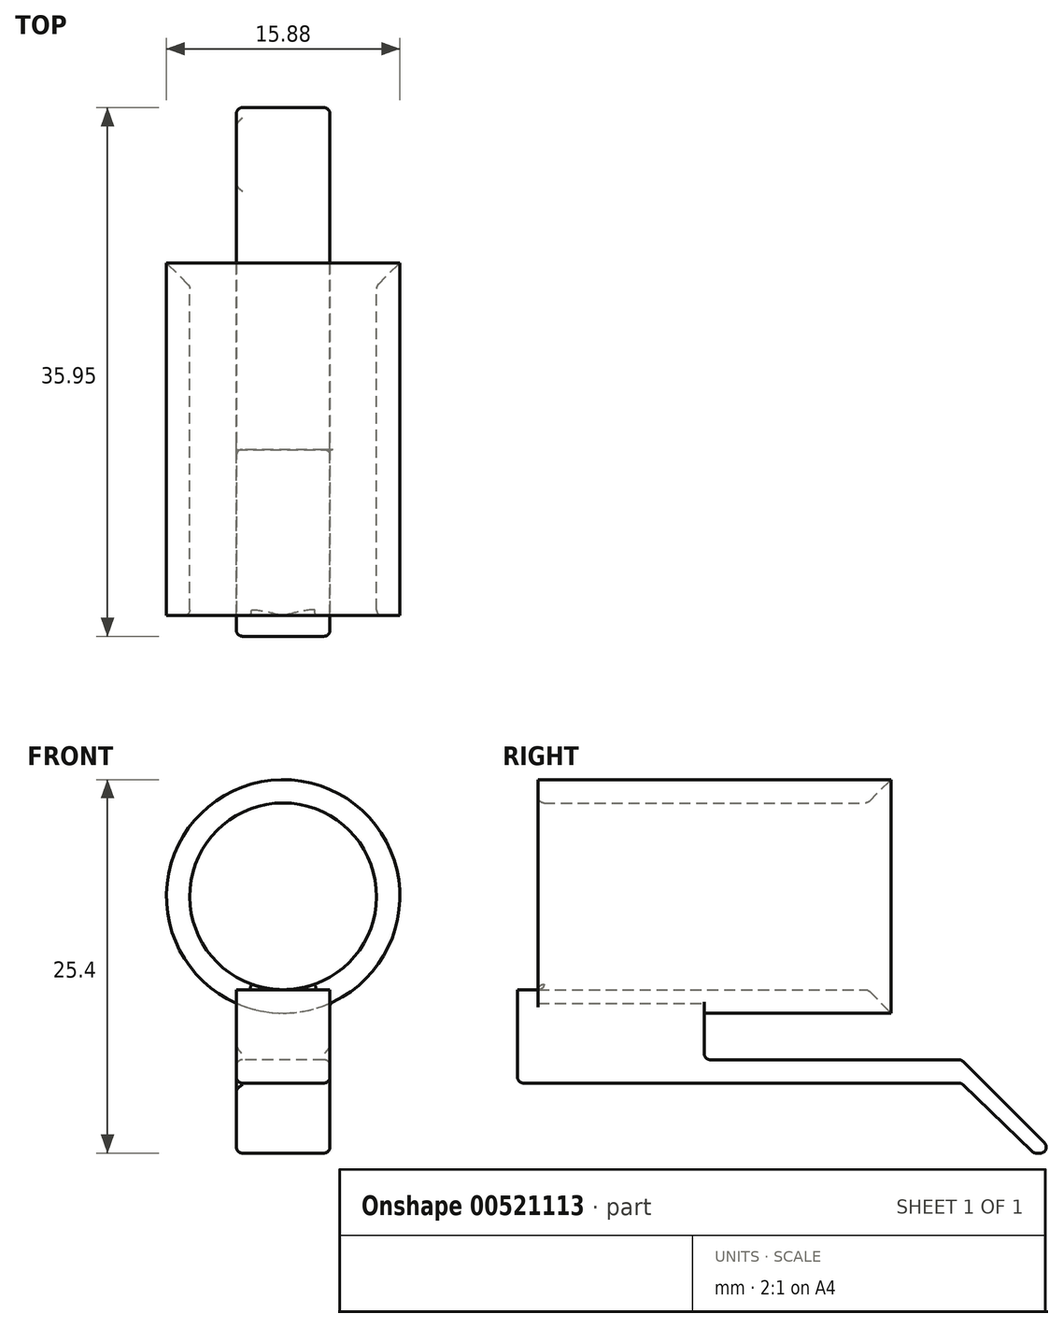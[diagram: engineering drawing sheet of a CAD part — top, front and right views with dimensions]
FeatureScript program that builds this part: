
annotation { "Feature Type Name" : "Feature", "Feature Type Description" : "" }
export const myFeature = defineFeature(function(context is Context, id is Id, definition is map)
    precondition{}
    {
        {
            var Q0;
            Q0=qCreatedBy(makeId("Front.planeOp"),FACE);
            var sketch = newSketch(context, id + "F0", { "sketchPlane" : qUnion([Q0])});
            skCircle(sketch, "E0", {"center": v(0, 0) * mm, "radius": 6.35 * mm});
            skCircle(sketch, "E1", {"center": v(0, 0) * mm, "radius": 7.94 * mm});
            skLineSegment(sketch, "E2", {"start": v(3.42, 5.35) * mm, "end": v(4.28, 6.69) * mm, "construction": true});
            skSolve(sketch);
        }
        {
            assignVariable(context, id + "F1", {"name" : "BarrelLenght", "anyValue" : 24});
        }
        {
            var Q0;
            Q0 = qSketchRegion(id + "F0", true);
            extrude(context, id + "F2", {"entities" : qUnion([Q0]), "depth" : (getVariable(context, 'BarrelLenght')) * mm, "offsetDistance" : 25.4 * mm});
        }
        {
            var Q0;
            Q0=qCreatedBy(makeId("Right.planeOp"),FACE);
            var sketch = newSketch(context, id + "F3", { "sketchPlane" : qUnion([Q0])});
            skLineSegment(sketch, "E3", {"start": v(0, -6.35) * mm, "end": v(-12.7, -6.35) * mm, "construction": true});
            skLineSegment(sketch, "E4", {"start": v(0, -6.35) * mm, "end": v(0, 0) * mm, "construction": true});
            skLineSegment(sketch, "E5.bottom", {"start": v(-12.7, -6.35) * mm, "end": v(-25.4, -6.35) * mm});
            skLineSegment(sketch, "E5.top", {"start": v(-12.7, -12.7) * mm, "end": v(-25.4, -12.7) * mm});
            skLineSegment(sketch, "E5.right", {"start": v(-25.4, -6.35) * mm, "end": v(-25.4, -12.7) * mm});
            skLineSegment(sketch, "E6.bottom", {"start": v(-12.7, -12.7) * mm, "end": v(0, -12.7) * mm});
            skLineSegment(sketch, "E6.top", {"start": v(-12.7, -11.11) * mm, "end": v(0, -11.11) * mm});
            skLineSegment(sketch, "E6.left", {"start": v(-12.7, -12.7) * mm, "end": v(-12.7, -11.11) * mm, "construction": true});
            skLineSegment(sketch, "E6.right", {"start": v(0, -12.7) * mm, "end": v(0, -11.11) * mm, "construction": true});
            skLineSegment(sketch, "E7", {"start": v(-12.7, -11.11) * mm, "end": v(-12.7, -6.35) * mm});
            skLineSegment(sketch, "E8.bottom", {"start": v(0, -6.35) * mm, "end": v(4.76, -6.35) * mm, "construction": true});
            skLineSegment(sketch, "E8.top", {"start": v(0, -11.11) * mm, "end": v(4.76, -11.11) * mm});
            skLineSegment(sketch, "E8.left", {"start": v(0, -6.35) * mm, "end": v(0, -11.11) * mm, "construction": true});
            skLineSegment(sketch, "E8.right", {"start": v(4.76, -6.35) * mm, "end": v(4.76, -11.11) * mm, "construction": true});
            skLineSegment(sketch, "E9.bottom", {"start": v(4.76, -11.11) * mm, "end": v(11.11, -11.11) * mm, "construction": true});
            skLineSegment(sketch, "E9.top", {"start": v(4.76, -17.46) * mm, "end": v(11.11, -17.46) * mm, "construction": true});
            skLineSegment(sketch, "E9.left", {"start": v(4.76, -11.11) * mm, "end": v(4.76, -17.46) * mm, "construction": true});
            skLineSegment(sketch, "E9.right", {"start": v(11.11, -11.11) * mm, "end": v(11.11, -17.46) * mm, "construction": true});
            skLineSegment(sketch, "E10", {"start": v(0, -12.7) * mm, "end": v(4.76, -12.7) * mm});
            skLineSegment(sketch, "E11", {"start": v(4.76, -11.11) * mm, "end": v(11.11, -17.46) * mm});
            skLineSegment(sketch, "E12.bottom", {"start": v(4.76, -17.46) * mm, "end": v(9.7, -17.46) * mm, "construction": true});
            skLineSegment(sketch, "E12.top", {"start": v(4.76, -12.7) * mm, "end": v(9.7, -12.7) * mm, "construction": true});
            skLineSegment(sketch, "E12.left", {"start": v(4.76, -17.46) * mm, "end": v(4.76, -12.7) * mm, "construction": true});
            skLineSegment(sketch, "E12.right", {"start": v(9.7, -17.46) * mm, "end": v(9.7, -12.7) * mm, "construction": true});
            skLineSegment(sketch, "E13", {"start": v(4.76, -12.7) * mm, "end": v(9.7, -17.46) * mm});
            skLineSegment(sketch, "E14", {"start": v(9.7, -17.46) * mm, "end": v(11.11, -17.46) * mm});
            skSolve(sketch);
        }
        {
            var Q0;
            Q0=makeQuery(id+"F3.imprint","IMPRINT",FACE,{"disambiguationData":[TD([[makeQuery(id+"F3.imprint","IMPRINT",EDGE,{"derivedFrom":sQuery(id+"F3.wireOp",EDGE,"E5.bottom")}),1.0]])]});
            extrude(context, id + "F4", {"entities" : qUnion([Q0]), "operationType" : NewBodyOperationType.ADD, "depth" : 6.35 * mm, "offsetDistance" : 25.4 * mm, "symmetric" : true});
        }
        {
            var Q0;
            Q0=makeQuery(id+"F2.opExtrude","CAP_EDGE",EDGE,{"disambiguationData":[OSD([sQuery(id+"F0.wireOp",EDGE,"E0")])],"isStart":true});
            chamfer(context, id + "F5", {"entities" : qUnion([Q0]), "width" : 1.59 * mm, "tangentPropagation" : true});
        }
        {
            var Q0;
            Q0=makeQuery(id+"F4.opExtrude","SWEPT_EDGE",EDGE,{"disambiguationData":[OSD([sQuery(id+"F3.wireOp",EDGE,"E6.top"),sQuery(id+"F3.wireOp",EDGE,"E7")])]});
            var Q1;
            Q1=makeQuery(id+"F4.opExtrude","CAP_EDGE",EDGE,{"disambiguationData":[OSD([sQuery(id+"F3.wireOp",EDGE,"E6.top"),sQuery(id+"F3.wireOp",EDGE,"E8.top")])],"isStart":false});
            var Q2;
            Q2=makeQuery(id+"F4.opExtrude","CAP_EDGE",EDGE,{"disambiguationData":[OSD([sQuery(id+"F3.wireOp",EDGE,"E6.top"),sQuery(id+"F3.wireOp",EDGE,"E8.top")])],"isStart":true});
            var Q3;
            Q3=makeQuery(id+"F4.opExtrude","CAP_EDGE",EDGE,{"disambiguationData":[OSD([sQuery(id+"F3.wireOp",EDGE,"E11")])],"isStart":true});
            var Q4;
            Q4=makeQuery(id+"F4.opExtrude","SWEPT_EDGE",EDGE,{"disambiguationData":[OSD([sQuery(id+"F3.wireOp",EDGE,"E8.top"),sQuery(id+"F3.wireOp",EDGE,"E11")])]});
            var Q5;
            Q5=makeQuery(id+"F4.opExtrude","CAP_EDGE",EDGE,{"disambiguationData":[OSD([sQuery(id+"F3.wireOp",EDGE,"E11")])],"isStart":false});
            var Q6;
            Q6=makeQuery(id+"F4.opExtrude","CAP_EDGE",EDGE,{"disambiguationData":[OSD([sQuery(id+"F3.wireOp",EDGE,"E13")])],"isStart":false});
            var Q7;
            Q7=makeQuery(id+"F4.opExtrude","SWEPT_FACE",FACE,{"disambiguationData":[OSD([sQuery(id+"F3.wireOp",EDGE,"E5.top"),sQuery(id+"F3.wireOp",EDGE,"E6.bottom"),sQuery(id+"F3.wireOp",EDGE,"E10")])]});
            var Q8;
            Q8=makeQuery(id+"F4.opExtrude","CAP_EDGE",EDGE,{"disambiguationData":[OSD([sQuery(id+"F3.wireOp",EDGE,"E5.right")])],"isStart":true});
            var Q9;
            Q9=makeQuery(id+"F4.opExtrude","CAP_EDGE",EDGE,{"disambiguationData":[OSD([sQuery(id+"F3.wireOp",EDGE,"E5.right")])],"isStart":false});
            var Q10;
            Q10=makeQuery(id+"F4.opExtrude","SWEPT_FACE",FACE,{"disambiguationData":[OSD([sQuery(id+"F3.wireOp",EDGE,"E14")])]});
            var Q11;
            Q11=makeQuery(id+"F4.boolean.opBoolean","INTERSECT",EDGE,{"derivedFrom":[makeQuery(id+"F2.opExtrude","SWEPT_FACE",FACE,{"disambiguationData":[OSD([sQuery(id+"F0.wireOp",EDGE,"E1")])]}),makeQuery(id+"F4.opExtrude","CAP_FACE",FACE,{"disambiguationData":[OSD([sQuery(id+"F3.wireOp",EDGE,"E5.bottom"),sQuery(id+"F3.wireOp",EDGE,"E5.top"),sQuery(id+"F3.wireOp",EDGE,"E5.right"),sQuery(id+"F3.wireOp",EDGE,"E6.bottom"),sQuery(id+"F3.wireOp",EDGE,"E6.top"),sQuery(id+"F3.wireOp",EDGE,"E7"),sQuery(id+"F3.wireOp",EDGE,"E8.top"),sQuery(id+"F3.wireOp",EDGE,"E10"),sQuery(id+"F3.wireOp",EDGE,"E11"),sQuery(id+"F3.wireOp",EDGE,"E13"),sQuery(id+"F3.wireOp",EDGE,"E14")])],"isStart":false})]});
            var Q12;
            Q12=makeQuery(id+"F2.opExtrude","SWEPT_FACE",FACE,{"disambiguationData":[OSD([sQuery(id+"F0.wireOp",EDGE,"E0")])]});
            fillet(context, id + "F6", {"entities" : qUnion([Q0, Q1, Q2, Q3, Q4, Q5, Q6, Q7, Q8, Q9, Q10, Q11, Q12]), "radius" : 0.4 * mm, "tangentPropagation" : true, "allowEdgeOverflow" : false});
        }
    });
